# Revit family: Toilet_Universal-Floor_Mount-Sloan-ST-2029_Series
name_source: partatom
category: Plumbing Fixtures
revit_build: Autodesk Revit 2014 (Build: 20130308_1515(x64)
units: mm (PartAtom-declared; Revit-internal decimal feet)

## types (4) — shared parameters
ADA Compliant = Yes
Assembly Code = D2010110
CW Connection = Yes
CWFU = 10
Default Elevation = 17"
Fixture Color = White
Flush Volume = 1.1 to 1.6gpf/4.2 to 6.0Lpf
Front of Bowl Dist. from Wall = 29 5/8"
HW Connection = No
High Efficiency = Yes
IAPMO Certificate = Green cUPC
Inlet Spud Size = 1 1/2"
Manufacturer = SLOAN
Material = Vitreous China-Sloan-White
Mounting = Floor Mount ADA
Price = Prices may vary. Please consult Sloan Rep for most up-to-date price list.
Product Documentation Link = https://specifications.sloan.com
Product URL = https://www.sloan.com
Revision Date = 6/1/2018
Spud Inlet Radius = 3/4"
Spud Location = Top Spud
URL = https://www.sloan.com
Vent Connection = No
WFU = 10
Waste Connection = Yes
Waste Connection Radius = 1 1/16"
zero-valued in all types: HWFU

## per-type parameters (varying)
| type | BPL | Description | Order Code | Toilet |
| ST-2029 | No | Floor Mounted ADA Top Spud Closet (PP2.0) | 2102029 | ST-2029 |
| ST-2029-STG | No | Floor Mounted ADA Top Spud Closet (PP2.0) with SloanTec hydrophobic antimicrobial glaze. | 2172029 | ST-2029 |
| ST-2029-BPL | Yes | Floor Mounted ADA Top Spud Closet (PP2.0) with bed pan lugs. | 2112029 | ST-2029 : ST-2029-BPL |
| ST-2029-BPL-STG | Yes | Floor Mounted ADA Top Spud Closet (PP2.0) with bedpan lug  with SloanTec hydrophobic antimicrobial glaze. | 20172020 | ST-2029 : ST-2029-BPL |

note: column(s) folded — value = type name in every type: Model

## geometry (parser evidence)
native form markers: Sweep x4
no freeform markers — native parametric forms only
